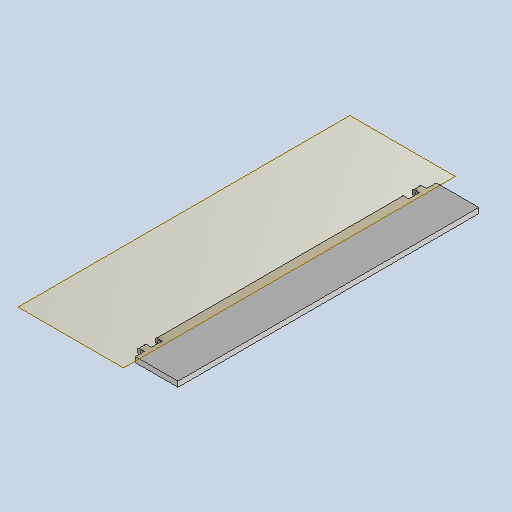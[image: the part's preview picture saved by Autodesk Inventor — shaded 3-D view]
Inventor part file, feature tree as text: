
AUTODESK INVENTOR PART (.ipt)
format: ipt  version: 2024 (Build 280153000, 153)  size: 296,448 bytes
history: native  units: mm
features: other x3, extrude x2, sketch x2, reference x2, plane x1, fillet x1
ambient origin geometry x8: Origin, YZ Plane, XZ Plane, XY Plane, X Axis, Y Axis, Z Axis, Center Point
bodies: Solid1 (feature_tree)
feature tree (11):
  plane  "Work Plane1"
  extrude  "Extrusion1"  Depth=24.0mm
  extrude  "Extrusion2"  Depth=1.0mm
  fillet  "Fillet1"  Radius=3.0mm
  sketch  "Sketch1"  dims[d0=0.5mm d1=24.0mm]
  reference  "Reference1"
  sketch  "Sketch2"  dims[d2=2.071487mm d3=2.5mm d4=3.0mm d5=0.0mm d6=2.0mm d7=2.5mm d8=1.5mm d9=0.0mm d10=0.0mm d11=1.0mm]
  reference  "Reference2"
  other  "<userpath> windows\Documents\Inventor\Robotska_roka\Assembly4.iam"
  other  "Assembly4.iam"
  other  "pokrow:1"
